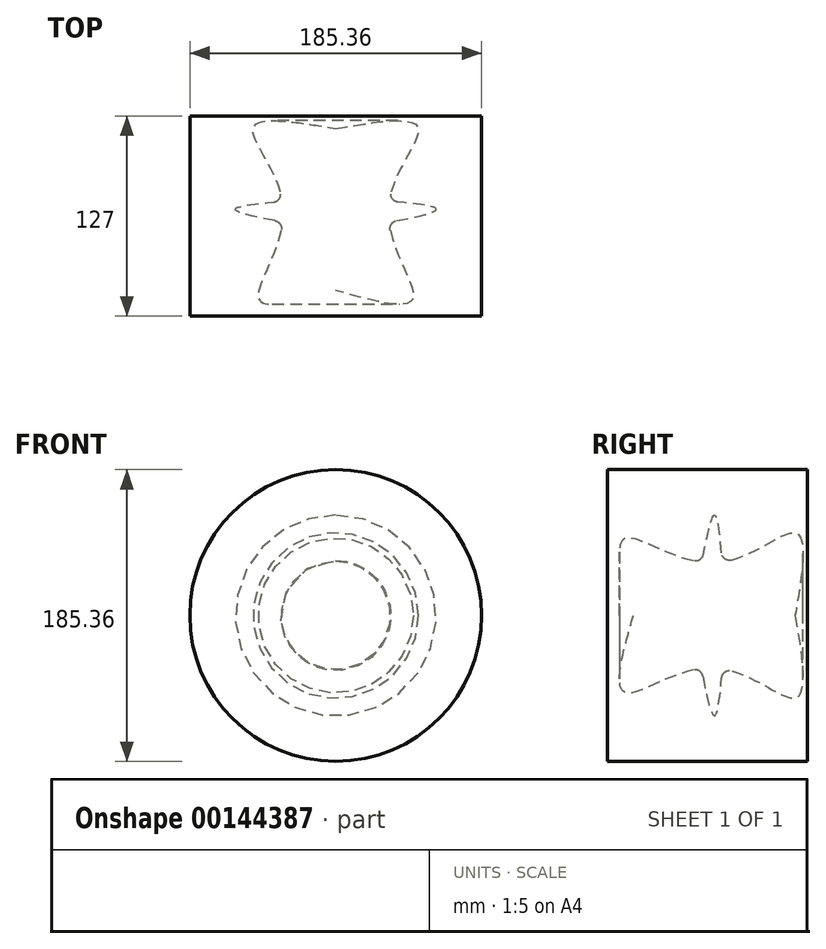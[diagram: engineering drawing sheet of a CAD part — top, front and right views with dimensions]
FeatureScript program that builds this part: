
annotation { "Feature Type Name" : "Feature", "Feature Type Description" : "" }
export const myFeature = defineFeature(function(context is Context, id is Id, definition is map)
    precondition{}
    {
        {
            var Q0;
            Q0=qCreatedBy(makeId("Top.planeOp"),FACE);
            var sketch = newSketch(context, id + "F0", { "sketchPlane" : qUnion([Q0])});
            skLineSegment(sketch, "E0", {"start": v(0, 65.53) * mm, "end": v(0, -66.06) * mm});
            skFitSpline(sketch, "E1", {"points": [v(0, 55.56) * mm, v(52.37, 56.1) * mm, v(33.22, 4.32) * mm, v(48.86, -52.58) * mm, v(0, -47.19) * mm], "startDerivative": vector(302.86, 51.59) * mm, "endDerivative": vector(-287.01, 81.48) * mm});
            skFitSpline(sketch, "E2", {"points": [v(0, 11.6) * mm, v(63.7, 4.32) * mm, v(0, -9.43) * mm], "startDerivative": vector(191.35, -11.44) * mm, "endDerivative": vector(-190.83, -30.6) * mm});
            skSolve(sketch);
        }
        {
            var Q0;
            Q0 = qSketchRegion(id + "F0", true);
            var Q1;
            Q1=sQuery(id+"F0.wireOp",EDGE,"E0");
            revolve(context, id + "F1", {"entities" : qUnion([Q0]), "axis" : qUnion([Q1]), "revolveType" : RevolveType.FULL});
        }
        {
            var Q0;
            {var subQ0=sQuery(id+"F0.wireOp",EDGE,"E2");var subQ1=sQuery(id+"F0.wireOp",EDGE,"E1");Q0=makeQuery(id+"F1.opRevolve","SWEPT_EDGE",EDGE,{"disambiguationData":[OSD([subQ1,subQ0]),TDD([makeQuery(id+"F0.imprint","INTERSECT",VERTEX,{"disambiguationData":[OD(0.0)],"derivedFrom":[subQ1,subQ0]})])]});}
            var Q1;
            {var subQ0=sQuery(id+"F0.wireOp",EDGE,"E2");var subQ1=sQuery(id+"F0.wireOp",EDGE,"E1");Q1=makeQuery(id+"F1.opRevolve","SWEPT_EDGE",EDGE,{"disambiguationData":[OSD([subQ1,subQ0]),TDD([makeQuery(id+"F0.imprint","INTERSECT",VERTEX,{"disambiguationData":[OD(1.0)],"derivedFrom":[subQ1,subQ0]})])]});}
            fillet(context, id + "F2", {"entities" : qUnion([Q0, Q1]), "radius" : 5.08 * mm, "tangentPropagation" : true, "allowEdgeOverflow" : false});
        }
        {
            var Q0;
            Q0=qCreatedBy(makeId("Front.planeOp"),FACE);
            var sketch = newSketch(context, id + "F3", { "sketchPlane" : qUnion([Q0])});
            skCircle(sketch, "E3", {"center": v(0, 0) * mm, "radius": 92.68 * mm});
            skSolve(sketch);
        }
        {
            var Q0;
            Q0 = qSketchRegion(id + "F3", true);
            extrude(context, id + "F4", {"entities" : qUnion([Q0]), "endBound" : BoundingType.SYMMETRIC, "depth" : 127 * mm});
        }
        {
            var Q0;
            Q0=makeQuery(id+"F1.opRevolve","SWEPT_BODY",BODY,{"disambiguationData":[OSD([sQuery(id+"F0.wireOp",EDGE,"E0"),sQuery(id+"F0.wireOp",EDGE,"E1"),sQuery(id+"F0.wireOp",EDGE,"E2")])]});
            var Q1;
            Q1=makeQuery(id+"F4.opExtrude","SWEPT_BODY",BODY,{"disambiguationData":[OSD([sQuery(id+"F3.wireOp",EDGE,"E3")])]});
            booleanBodies(context, id + "F5", {"operationType" : BooleanOperationType.SUBTRACTION, "tools" : qUnion([Q0]), "targets" : qUnion([Q1])});
        }
    });
